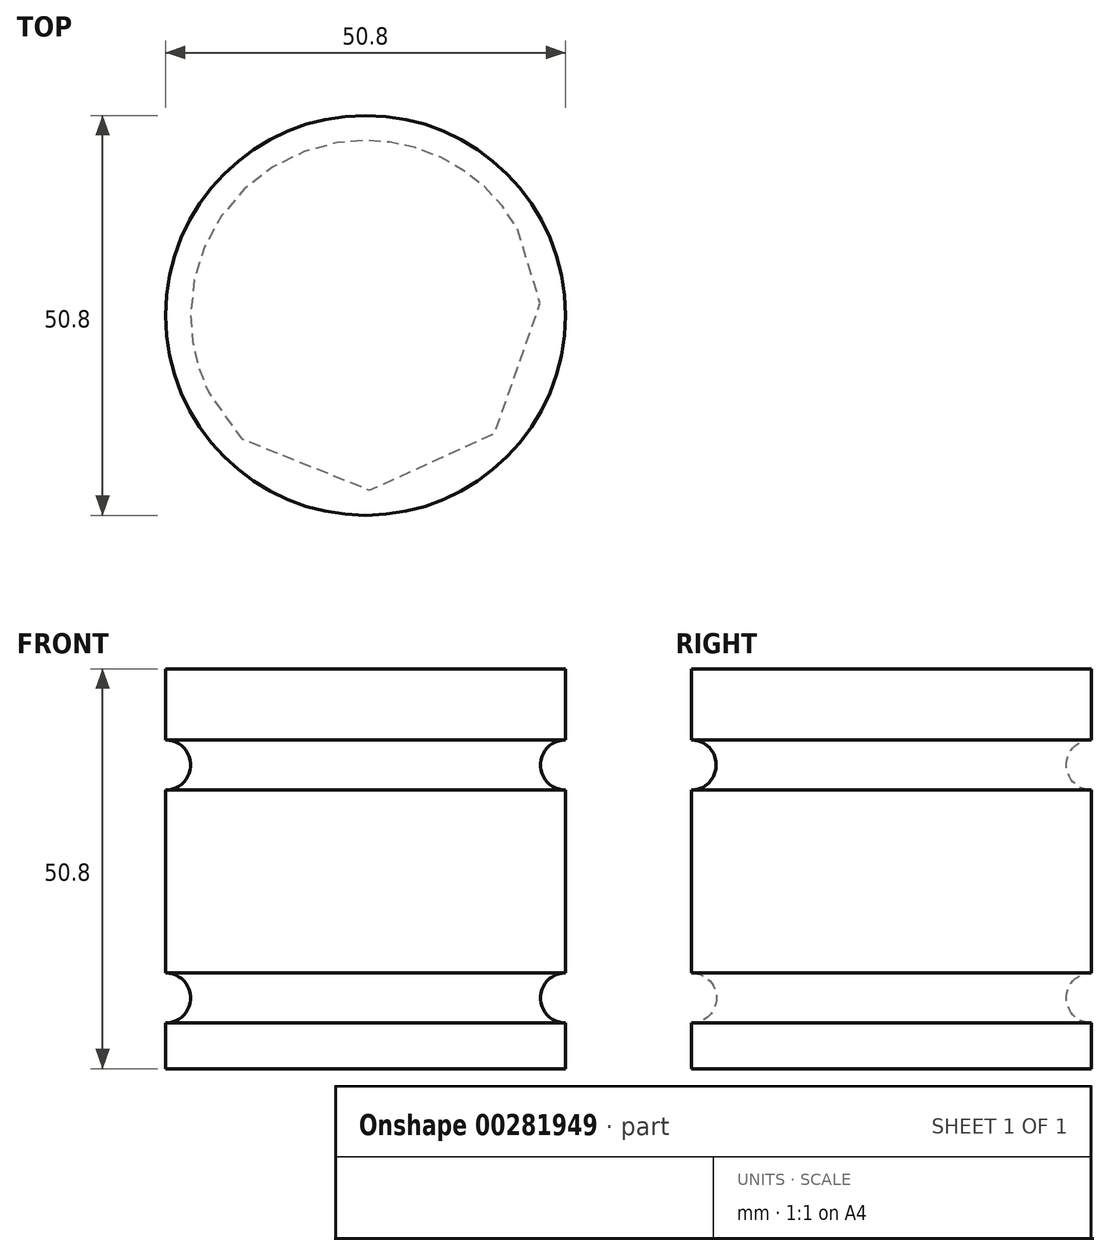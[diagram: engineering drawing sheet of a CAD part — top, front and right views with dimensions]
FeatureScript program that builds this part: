
annotation { "Feature Type Name" : "Feature", "Feature Type Description" : "" }
export const myFeature = defineFeature(function(context is Context, id is Id, definition is map)
    precondition{}
    {
        {
            var Q0;
            Q0=qCreatedBy(makeId("Front.planeOp"),FACE);
            var sketch = newSketch(context, id + "F0", { "sketchPlane" : qUnion([Q0])});
            skLineSegment(sketch, "E0.bottom", {"start": v(0, 0) * mm, "end": v(-25.4, 0) * mm});
            skLineSegment(sketch, "E0.top", {"start": v(0, 50.8) * mm, "end": v(-25.4, 50.8) * mm});
            skLineSegment(sketch, "E0.left", {"start": v(0, 0) * mm, "end": v(0, 5.8) * mm});
            skLineSegment(sketch, "E0.right", {"start": v(-25.4, 0) * mm, "end": v(-25.4, 50.8) * mm});
            skArc(sketch, "E1", {"start": v(0, 41.75) * mm, "mid": v(-3.18, 38.57) * mm, "end": v(0, 35.4) * mm});
            skArc(sketch, "E2", {"start": v(0, 12.15) * mm, "mid": v(-3.18, 8.98) * mm, "end": v(0, 5.8) * mm});
            skLineSegment(sketch, "E3.trimOffspring", {"start": v(0, 12.15) * mm, "end": v(0, 35.4) * mm});
            skLineSegment(sketch, "E4.trimOffspring", {"start": v(0, 41.75) * mm, "end": v(0, 50.8) * mm});
            skSolve(sketch);
        }
        {
            var Q0;
            Q0=makeQuery(id+"F0.imprint","IMPRINT",FACE,{"disambiguationData":[TD([[makeQuery(id+"F0.imprint","IMPRINT",EDGE,{"derivedFrom":sQuery(id+"F0.wireOp",EDGE,"E0.bottom")}),-1.0]])]});
            var Q1;
            Q1=sQuery(id+"F0.wireOp",EDGE,"E0.right");
            revolve(context, id + "F1", {"entities" : qUnion([Q0]), "axis" : qUnion([Q1]), "revolveType" : RevolveType.FULL});
        }
    });
